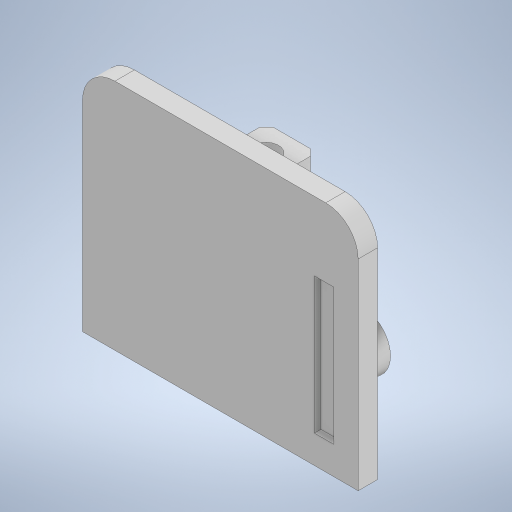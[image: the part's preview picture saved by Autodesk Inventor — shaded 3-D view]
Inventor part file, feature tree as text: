
AUTODESK INVENTOR PART (.ipt)
format: ipt  version: 2023 (Build 270158000, 158)  size: 321,536 bytes
history: native  units: mm
features: extrude x7, sketch x7, other x2, pattern_linear x2, chamfer x2, projected_geometry x2, fillet x1
ambient origin geometry x8: Origin, YZ Plane, XZ Plane, XY Plane, X Axis, Y Axis, Z Axis, Center Point
bodies: Body1 (feature_tree)
feature tree (23):
  other  "솔리드1"
  extrude  "돌출1"  Depth=42.5mm
  fillet  "모깎기1"  Radius=36.25mm
  other  "작업 평면1"
  extrude  "돌출2"  Depth=3.0mm TaperAngle=0.0deg
  pattern_linear  "직사각형 패턴1"  Spacing1=5.0mm  [1 undecoded]
  extrude  "돌출3"  [1 undecoded]
  extrude  "돌출4"  Depth=4.0mm
  extrude  "돌출5"  Depth=4.0mm
  chamfer  "모따기1"  Distance=8.0mm
  extrude  "돌출6"  Depth=10.0mm
  extrude  "돌출9"  Depth=2.0mm TaperAngle=0.0deg
  chamfer  "모따기3"  Distance=22.5mm
  pattern_linear  "직사각형 패턴2"  Spacing1=15.8mm  [1 undecoded]
  sketch  "스케치1"
  sketch  "스케치2"
  sketch  "스케치3"
  sketch  "스케치4"
  sketch  "스케치5"
  sketch  "스케치6"
  projected_geometry  "투영된 루프1"
  projected_geometry  "투영된 루프2"
  sketch  "스케치9"
note: 3 required parameter values undecoded (feature->parameter linkage not recoverable at this tier; creation-order binding heuristic only, values carry confidence <= 0.55)
